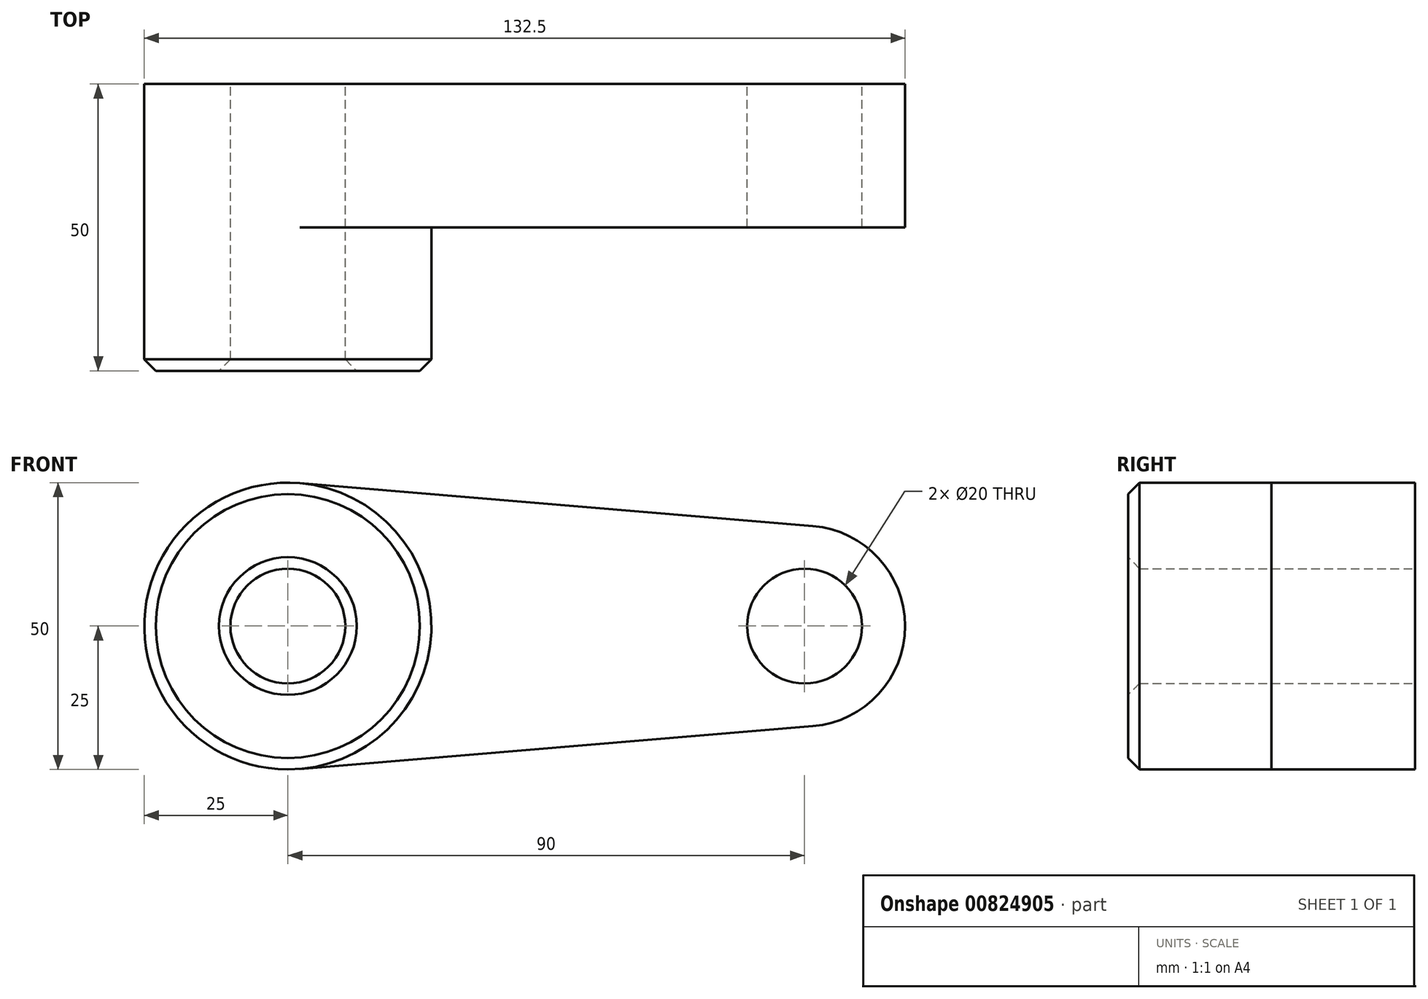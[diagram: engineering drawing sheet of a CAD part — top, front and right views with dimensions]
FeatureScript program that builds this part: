
annotation { "Feature Type Name" : "Feature", "Feature Type Description" : "" }
export const myFeature = defineFeature(function(context is Context, id is Id, definition is map)
    precondition{}
    {
        {
            var Q0;
            Q0=qCreatedBy(makeId("Front.planeOp"),FACE);
            var sketch = newSketch(context, id + "F0", { "sketchPlane" : qUnion([Q0])});
            skCircle(sketch, "E0", {"center": v(0, 0) * mm, "radius": 25 * mm});
            skCircle(sketch, "E1", {"center": v(90, 0) * mm, "radius": 17.5 * mm});
            skLineSegment(sketch, "E2", {"start": v(2.08, 24.91) * mm, "end": v(91.46, 17.44) * mm});
            skLineSegment(sketch, "E3", {"start": v(2.08, -24.91) * mm, "end": v(91.46, -17.44) * mm});
            skCircle(sketch, "E4", {"center": v(0, 0) * mm, "radius": 10 * mm});
            skCircle(sketch, "E5", {"center": v(90, 0) * mm, "radius": 10 * mm});
            skSolve(sketch);
        }
        {
            var Q0;
            Q0 = qSketchRegion(id + "F0", true);
            extrude(context, id + "F1", {"entities" : qUnion([Q0]), "depth" : 25 * mm, "offsetDistance" : 25 * mm});
        }
        {
            var Q0;
            Q0=makeQuery(id+"F0.imprint","IMPRINT",FACE,{"disambiguationData":[TD([[makeQuery(id+"F0.imprint","IMPRINT",EDGE,{"derivedFrom":sQuery(id+"F0.wireOp",EDGE,"E4")}),-1.0]])]});
            extrude(context, id + "F2", {"entities" : qUnion([Q0]), "operationType" : NewBodyOperationType.ADD, "depth" : 50 * mm, "offsetDistance" : 25 * mm});
        }
        {
            var Q0;
            Q0=makeQuery(id+"F2.opExtrude","CAP_FACE",FACE,{"disambiguationData":[OSD([sQuery(id+"F0.wireOp",EDGE,"E0"),sQuery(id+"F0.wireOp",EDGE,"E4")])],"isStart":false});
            chamfer(context, id + "F3", {"entities" : qUnion([Q0]), "width" : 2 * mm, "tangentPropagation" : true});
        }
    });
